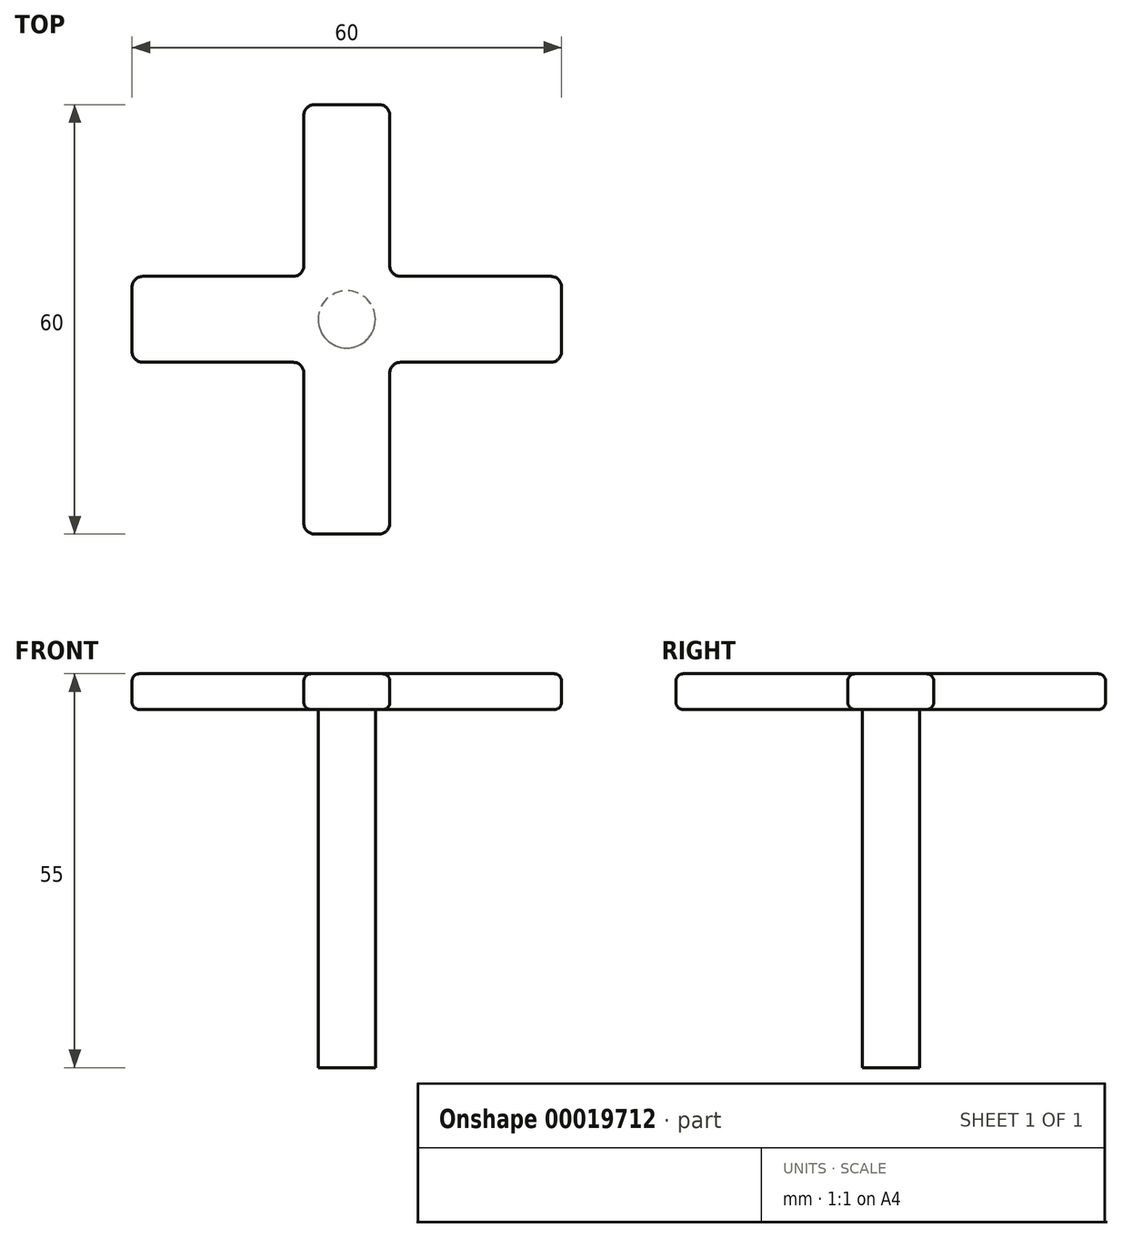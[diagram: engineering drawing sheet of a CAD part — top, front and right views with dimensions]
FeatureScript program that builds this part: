
annotation { "Feature Type Name" : "Feature", "Feature Type Description" : "" }
export const myFeature = defineFeature(function(context is Context, id is Id, definition is map)
    precondition{}
    {
        {
            var Q0;
            Q0=qCreatedBy(makeId("Top.planeOp"),FACE);
            var sketch = newSketch(context, id + "F0", { "sketchPlane" : qUnion([Q0])});
            skLineSegment(sketch, "E0", {"start": v(30, 0) * mm, "end": v(30, 4.5) * mm});
            skLineSegment(sketch, "E1", {"start": v(28.5, 6) * mm, "end": v(7.5, 6) * mm});
            skLineSegment(sketch, "E2", {"start": v(6, 7.5) * mm, "end": v(6, 28.5) * mm});
            skLineSegment(sketch, "E3", {"start": v(4.5, 30) * mm, "end": v(0, 30) * mm});
            skLineSegment(sketch, "E4", {"start": v(6, 6) * mm, "end": v(6, 0) * mm, "construction": true});
            skLineSegment(sketch, "E5", {"start": v(6, 6) * mm, "end": v(0, 6) * mm, "construction": true});
            skLineSegment(sketch, "E6", {"start": v(0, 30) * mm, "end": v(0, 0) * mm, "construction": true});
            skLineSegment(sketch, "E7", {"start": v(0, 0) * mm, "end": v(30, 0) * mm, "construction": true});
            skPoint(sketch, "E8.visualSharp", {"position": v(6, 30) * mm});
            skArc(sketch, "E8.filletArc", {"start": v(6, 28.5) * mm, "mid": v(5.56, 29.56) * mm, "end": v(4.5, 30) * mm});
            skPoint(sketch, "E9.visualSharp", {"position": v(6, 6) * mm});
            skArc(sketch, "E9.filletArc", {"start": v(6, 7.5) * mm, "mid": v(6.44, 6.44) * mm, "end": v(7.5, 6) * mm});
            skPoint(sketch, "E10.visualSharp", {"position": v(30, 6) * mm});
            skArc(sketch, "E10.filletArc", {"start": v(30, 4.5) * mm, "mid": v(29.56, 5.56) * mm, "end": v(28.5, 6) * mm});
            skLineSegment(sketch, "E11.MirrorCS", {"start": v(28.5, -6) * mm, "end": v(7.5, -6) * mm});
            skArc(sketch, "E12.MirrorCS", {"start": v(30, -4.5) * mm, "mid": v(29.56, -5.56) * mm, "end": v(28.5, -6) * mm});
            skLineSegment(sketch, "E13.MirrorCS", {"start": v(30, 0) * mm, "end": v(30, -4.5) * mm});
            skArc(sketch, "E14.MirrorCS", {"start": v(6, -7.5) * mm, "mid": v(6.44, -6.44) * mm, "end": v(7.5, -6) * mm});
            skLineSegment(sketch, "E15.MirrorCS", {"start": v(4.5, -30) * mm, "end": v(0, -30) * mm});
            skArc(sketch, "E16.MirrorCS", {"start": v(6, -28.5) * mm, "mid": v(5.56, -29.56) * mm, "end": v(4.5, -30) * mm});
            skLineSegment(sketch, "E17.MirrorCS", {"start": v(6, -7.5) * mm, "end": v(6, -28.5) * mm});
            skArc(sketch, "E18.MirrorCS", {"start": v(-6, -28.5) * mm, "mid": v(-5.56, -29.56) * mm, "end": v(-4.5, -30) * mm});
            skArc(sketch, "E19.MirrorCS", {"start": v(-30, -4.5) * mm, "mid": v(-29.56, -5.56) * mm, "end": v(-28.5, -6) * mm});
            skLineSegment(sketch, "E20.MirrorCS", {"start": v(-30, 0) * mm, "end": v(-30, -4.5) * mm});
            skArc(sketch, "E21.MirrorCS", {"start": v(-6, 7.5) * mm, "mid": v(-6.44, 6.44) * mm, "end": v(-7.5, 6) * mm});
            skLineSegment(sketch, "E22.MirrorCS", {"start": v(-4.5, -30) * mm, "end": v(0, -30) * mm});
            skLineSegment(sketch, "E23.MirrorCS", {"start": v(-28.5, 6) * mm, "end": v(-7.5, 6) * mm});
            skLineSegment(sketch, "E24.MirrorCS", {"start": v(-28.5, -6) * mm, "end": v(-7.5, -6) * mm});
            skLineSegment(sketch, "E25.MirrorCS", {"start": v(-4.5, 30) * mm, "end": v(0, 30) * mm});
            skArc(sketch, "E26.MirrorCS", {"start": v(-6, 28.5) * mm, "mid": v(-5.56, 29.56) * mm, "end": v(-4.5, 30) * mm});
            skArc(sketch, "E27.MirrorCS", {"start": v(-6, -7.5) * mm, "mid": v(-6.44, -6.44) * mm, "end": v(-7.5, -6) * mm});
            skLineSegment(sketch, "E28.MirrorCS", {"start": v(-6, -7.5) * mm, "end": v(-6, -28.5) * mm});
            skArc(sketch, "E29.MirrorCS", {"start": v(-30, 4.5) * mm, "mid": v(-29.56, 5.56) * mm, "end": v(-28.5, 6) * mm});
            skLineSegment(sketch, "E30.MirrorCS", {"start": v(-30, 0) * mm, "end": v(-30, 4.5) * mm});
            skLineSegment(sketch, "E31.MirrorCS", {"start": v(-6, 7.5) * mm, "end": v(-6, 28.5) * mm});
            skSolve(sketch);
        }
        {
            var Q0;
            Q0 = qSketchRegion(id + "F0", true);
            extrude(context, id + "F1", {"entities" : qUnion([Q0]), "depth" : 5 * mm});
        }
        {
            var Q0;
            Q0=makeQuery(id+"F1.opExtrude","CAP_EDGE",EDGE,{"disambiguationData":[OSD([sQuery(id+"F0.wireOp",EDGE,"E17.MirrorCS")])],"isStart":false});
            fillet(context, id + "F2", {"entities" : qUnion([Q0]), "radius" : 1 * mm, "tangentPropagation" : true, "allowEdgeOverflow" : false});
        }
        {
            var Q0;
            Q0=makeQuery(id+"F1.opExtrude","CAP_EDGE",EDGE,{"disambiguationData":[OSD([sQuery(id+"F0.wireOp",EDGE,"E17.MirrorCS")])],"isStart":true});
            fillet(context, id + "F3", {"entities" : qUnion([Q0]), "radius" : 1 * mm, "tangentPropagation" : true, "allowEdgeOverflow" : false});
        }
        {
            var Q0;
            Q0=makeQuery(id+"F1.opExtrude","CAP_FACE",FACE,{"disambiguationData":[OSD([sQuery(id+"F0.wireOp",EDGE,"E0"),sQuery(id+"F0.wireOp",EDGE,"E1"),sQuery(id+"F0.wireOp",EDGE,"E2"),sQuery(id+"F0.wireOp",EDGE,"E3"),sQuery(id+"F0.wireOp",EDGE,"E8.filletArc"),sQuery(id+"F0.wireOp",EDGE,"E9.filletArc"),sQuery(id+"F0.wireOp",EDGE,"E10.filletArc"),sQuery(id+"F0.wireOp",EDGE,"E11.MirrorCS"),sQuery(id+"F0.wireOp",EDGE,"E12.MirrorCS"),sQuery(id+"F0.wireOp",EDGE,"E13.MirrorCS"),sQuery(id+"F0.wireOp",EDGE,"E14.MirrorCS"),sQuery(id+"F0.wireOp",EDGE,"E15.MirrorCS"),sQuery(id+"F0.wireOp",EDGE,"E16.MirrorCS"),sQuery(id+"F0.wireOp",EDGE,"E17.MirrorCS"),sQuery(id+"F0.wireOp",EDGE,"E18.MirrorCS"),sQuery(id+"F0.wireOp",EDGE,"E19.MirrorCS"),sQuery(id+"F0.wireOp",EDGE,"E20.MirrorCS"),sQuery(id+"F0.wireOp",EDGE,"E21.MirrorCS"),sQuery(id+"F0.wireOp",EDGE,"E22.MirrorCS"),sQuery(id+"F0.wireOp",EDGE,"E23.MirrorCS"),sQuery(id+"F0.wireOp",EDGE,"E24.MirrorCS"),sQuery(id+"F0.wireOp",EDGE,"E25.MirrorCS"),sQuery(id+"F0.wireOp",EDGE,"E26.MirrorCS"),sQuery(id+"F0.wireOp",EDGE,"E27.MirrorCS"),sQuery(id+"F0.wireOp",EDGE,"E28.MirrorCS"),sQuery(id+"F0.wireOp",EDGE,"E29.MirrorCS"),sQuery(id+"F0.wireOp",EDGE,"E30.MirrorCS"),sQuery(id+"F0.wireOp",EDGE,"E31.MirrorCS")])],"isStart":true});
            var sketch = newSketch(context, id + "F4", { "sketchPlane" : qUnion([Q0])});
            skLineSegment(sketch, "E32", {"start": v(0, 29) * mm, "end": v(0, -29) * mm, "construction": true});
            skLineSegment(sketch, "E33", {"start": v(29, 0) * mm, "end": v(-29, 0) * mm, "construction": true});
            skCircle(sketch, "E34", {"center": v(0, 0) * mm, "radius": 4 * mm});
            skSolve(sketch);
        }
        {
            var Q0;
            Q0 = qSketchRegion(id + "F4", true);
            extrude(context, id + "F5", {"entities" : qUnion([Q0]), "operationType" : NewBodyOperationType.ADD, "depth" : 50 * mm});
        }
    });
